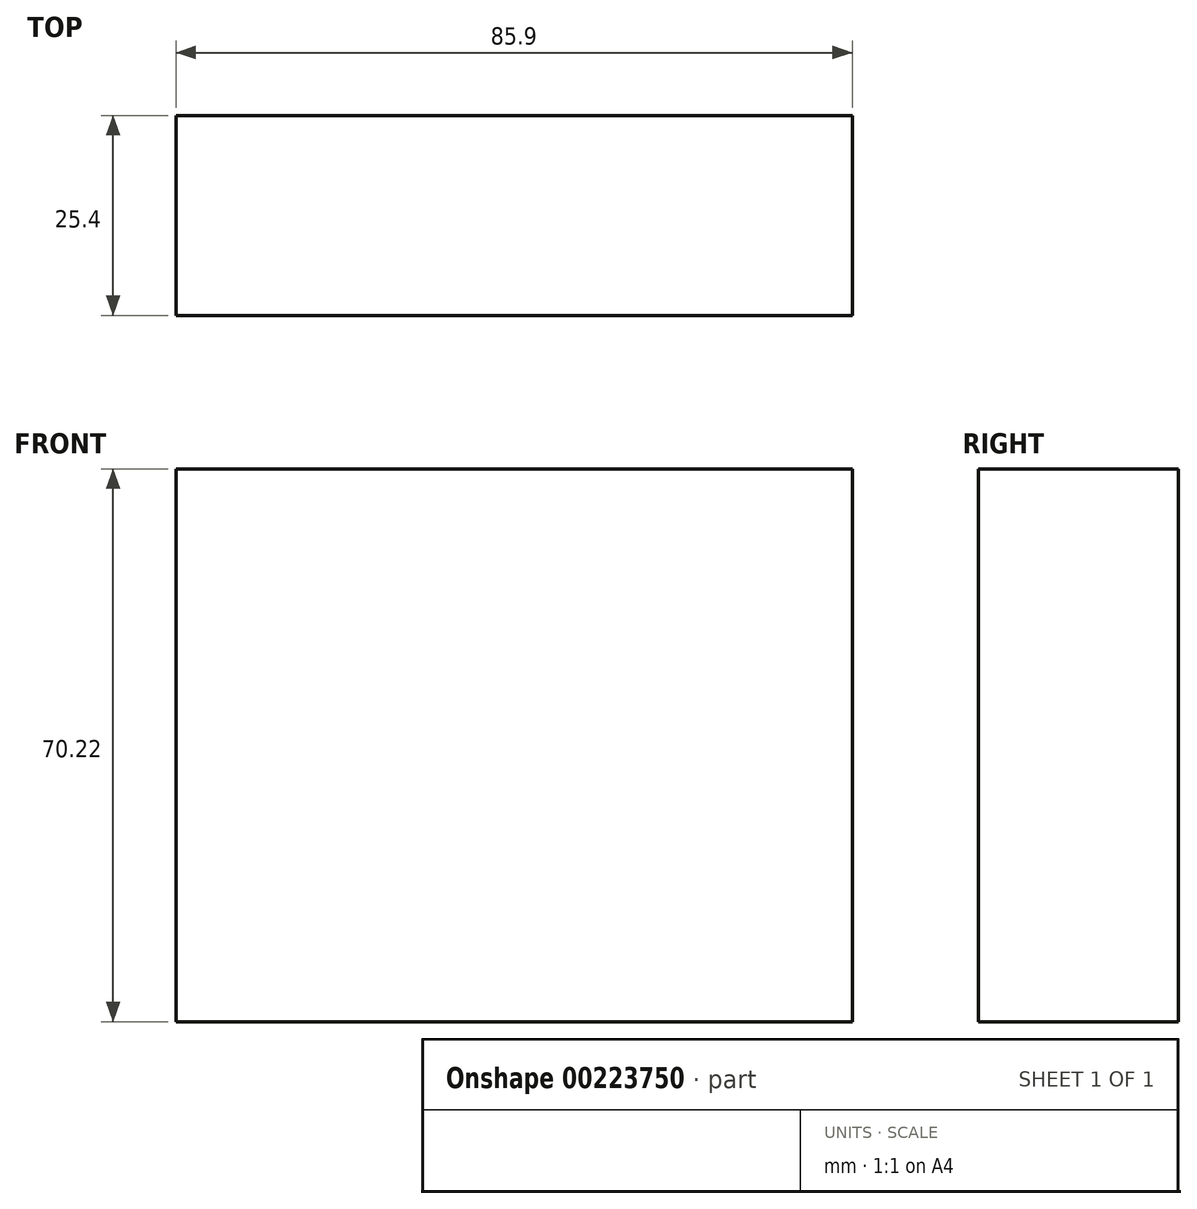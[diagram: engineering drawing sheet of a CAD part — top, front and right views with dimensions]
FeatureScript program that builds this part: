
annotation { "Feature Type Name" : "Feature", "Feature Type Description" : "" }
export const myFeature = defineFeature(function(context is Context, id is Id, definition is map)
    precondition{}
    {
        {
            var Q0;
            Q0=qCreatedBy(makeId("Front.planeOp"),FACE);
            var sketch = newSketch(context, id + "F0", { "sketchPlane" : qUnion([Q0])});
            skLineSegment(sketch, "E0.bottom", {"start": v(0, 0) * mm, "end": v(85.9, 0) * mm});
            skLineSegment(sketch, "E0.top", {"start": v(0, -70.22) * mm, "end": v(85.9, -70.22) * mm});
            skLineSegment(sketch, "E0.left", {"start": v(0, 0) * mm, "end": v(0, -70.22) * mm});
            skLineSegment(sketch, "E0.right", {"start": v(85.9, 0) * mm, "end": v(85.9, -70.22) * mm});
            skSolve(sketch);
        }
        {
            var Q0;
            Q0=makeQuery(id+"F0.imprint","IMPRINT",FACE,{"disambiguationData":[TD([[makeQuery(id+"F0.imprint","IMPRINT",EDGE,{"derivedFrom":sQuery(id+"F0.wireOp",EDGE,"E0.bottom")}),-1.0]])]});
            extrude(context, id + "F1", {"entities" : qUnion([Q0]), "depth" : 25.4 * mm});
        }
    });
